# Revit family: Pressure_Balance_Rough_Valve-GROHE-35114000
name_source: partatom
category: Plumbing Fixtures
revit_build: Autodesk Revit 2016 (Build: 20150714_1515(x64)
units: mm (PartAtom-declared; Revit-internal decimal feet)

## family parameters
Cut with Voids When Loaded = Yes
Host = Face
OmniClass Number = 23.45.05.14.17
OmniClass Title = Showers
Part Type = Normal
Room Calculation Point = No
Round Connector Dimension = Use Diameter
Shared = Yes

## types (2) — shared parameters
Assembly Code = D2020300
CW Connection = Yes
CWFU = 3
Connection CW Inlet Description = 1/2” CPVC Connection Inlet
Connection HW Inlet Description = 1/2” CPVC Connection Inlet
Connection Size = 1/2"
Default Elevation = 0"
Dept From Wall Face To COFC = 1"
Dept From Wall Face To Outlet = 2"
Description = Pressure Balance Valve Rough with CPVC with Service Stops
Finish = DZR_Brass-Grohe
HW Connection = Yes
HWFU = 3
Hot Inlet To Cold Inlet Width = 6 5/8"
Inlet To Center = 3 5/16"
Inlet to Wall = 1"
Installation Type = Wall Mounted
Manufacturer = Grohe
Material = DZR_Brass-Grohe
Model = 35114000
Outlet To Center = 1 13/16"
Outlet to Outlet = 3 5/8"
Outlet to Wall = 2"
Plaster Guard = Yes
Price = Prices may vary. Please consult Manufacturer Representative for most up-to-date price list.
ScrewDriver Stop = Yes
Shower Outlet To Spout Outlet Width = 3 5/8"
Specification = 1/2in CPVC inlets; 1/2in Universal outlets; Includes plug for 3-port installation; Universal connection is 1/2” male threads by copper sweat; Flush plug included; Can be tested using flush plug with air (200 psi) or water 300 psi; Made of DZR Brass; Service stops; Cartridge ships with the trim
URL = www.grohe.ca
Vent Connection = No
WFU = 4
Waste Connection = No
Water Connection Diameter = 1/2"

## per-type parameters (varying)
| type | Connection Outlet Description |
| GROHSAFE 3.0 - 35114000 1/2" Copper Sweat Outlet | 1/2" Copper Sweat Connection Outlet |
| GROHSAFE 3.0 - 35114000 1/2" NPT Outlet | 1/2" NPT Connection Outlet |

## geometry (parser evidence)
native form markers: Sweep x2
no freeform markers — native parametric forms only
